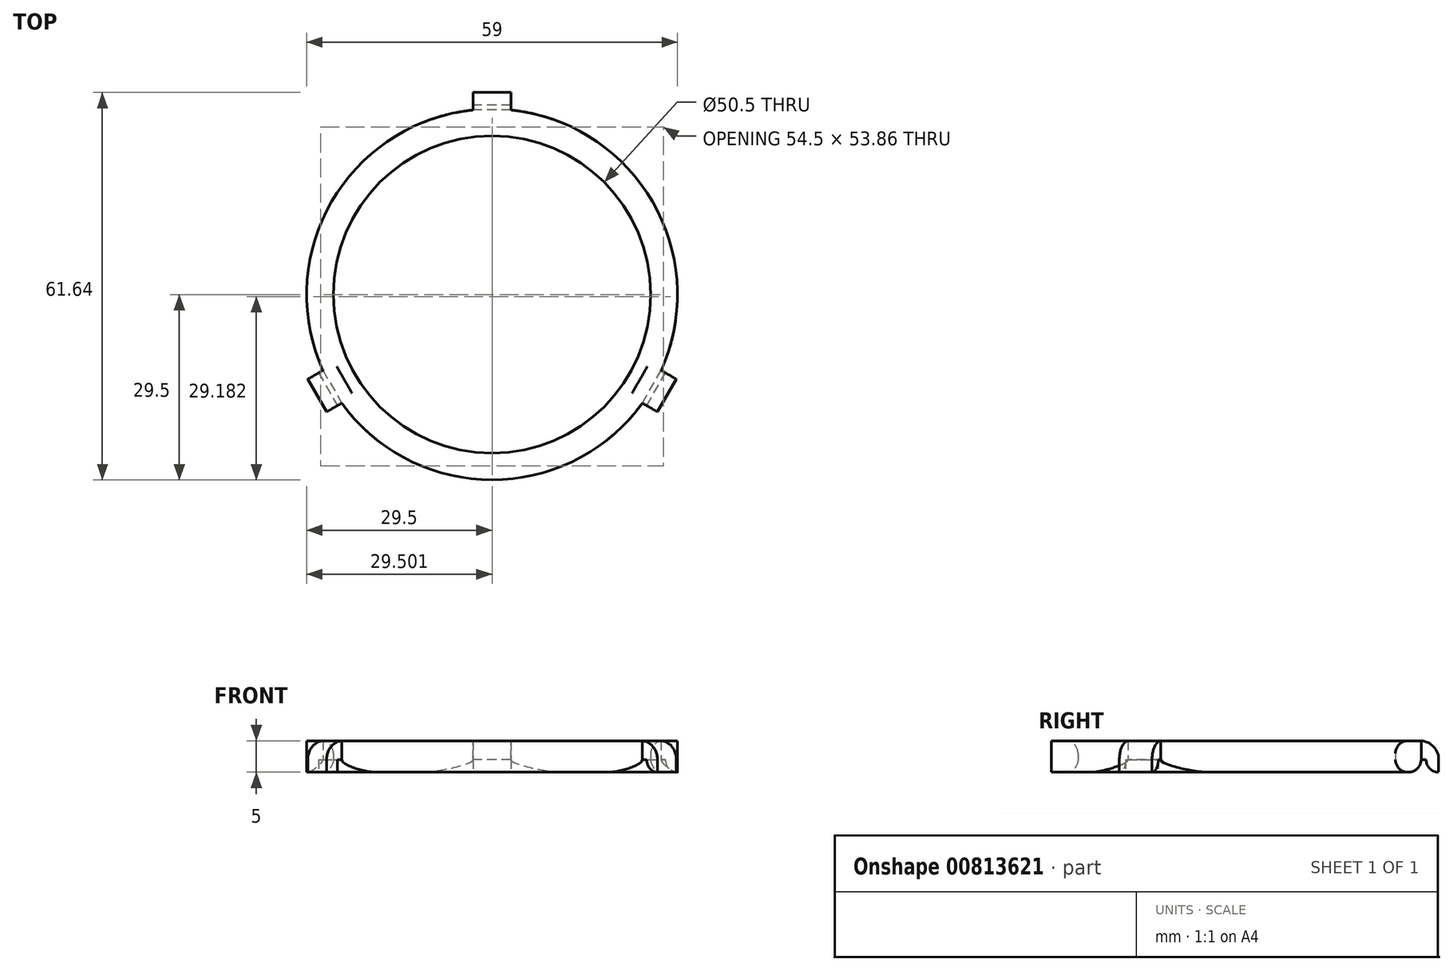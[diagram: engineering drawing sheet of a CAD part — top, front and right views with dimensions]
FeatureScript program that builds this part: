
annotation { "Feature Type Name" : "Feature", "Feature Type Description" : "" }
export const myFeature = defineFeature(function(context is Context, id is Id, definition is map)
    precondition{}
    {
        {
            var Q0;
            Q0=qCreatedBy(makeId("Top.planeOp"),FACE);
            var sketch = newSketch(context, id + "F0", { "sketchPlane" : qUnion([Q0])});
            skCircle(sketch, "E0", {"center": v(0, 0) * mm, "radius": 25.25 * mm});
            skCircle(sketch, "E1", {"center": v(0, 0) * mm, "radius": 29.5 * mm});
            skSolve(sketch);
        }
        {
            var Q0;
            Q0 = qSketchRegion(id + "F0", true);
            extrude(context, id + "F1", {"entities" : qUnion([Q0]), "depth" : 5 * mm, "offsetDistance" : 25 * mm});
        }
        {
            var Q0;
            Q0=makeQuery(id+"F1.opExtrude","CAP_EDGE",EDGE,{"disambiguationData":[OSD([sQuery(id+"F0.wireOp",EDGE,"E0")])],"isStart":false});
            var Q1;
            Q1=makeQuery(id+"F1.opExtrude","CAP_EDGE",EDGE,{"disambiguationData":[OSD([sQuery(id+"F0.wireOp",EDGE,"E0")])],"isStart":true});
            fillet(context, id + "F2", {"entities" : qUnion([Q0, Q1]), "radius" : 2 * mm, "tangentPropagation" : true, "allowEdgeOverflow" : false});
        }
        {
            var Q0;
            Q0=qCreatedBy(makeId("Top.planeOp"),FACE);
            var sketch = newSketch(context, id + "F3", { "sketchPlane" : qUnion([Q0])});
            skLineSegment(sketch, "E2.bottom", {"start": v(-3, 32.14) * mm, "end": v(3, 32.14) * mm});
            skLineSegment(sketch, "E2.top", {"start": v(-3, 27.14) * mm, "end": v(3, 27.14) * mm});
            skLineSegment(sketch, "E2.left", {"start": v(-3, 32.14) * mm, "end": v(-3, 27.14) * mm});
            skLineSegment(sketch, "E2.right", {"start": v(3, 32.14) * mm, "end": v(3, 27.14) * mm});
            skLineSegment(sketch, "E3.1.0", {"start": v(-26.33, -18.67) * mm, "end": v(-29.33, -13.47) * mm});
            skLineSegment(sketch, "E3.1.1", {"start": v(-22, -16.17) * mm, "end": v(-25, -10.97) * mm});
            skLineSegment(sketch, "E3.1.2", {"start": v(-26.33, -18.67) * mm, "end": v(-22, -16.17) * mm});
            skLineSegment(sketch, "E3.1.3", {"start": v(-29.33, -13.47) * mm, "end": v(-25, -10.97) * mm});
            skLineSegment(sketch, "E3.2.0", {"start": v(29.33, -13.47) * mm, "end": v(26.33, -18.67) * mm});
            skLineSegment(sketch, "E3.2.1", {"start": v(25, -10.97) * mm, "end": v(22, -16.17) * mm});
            skLineSegment(sketch, "E3.2.2", {"start": v(29.33, -13.47) * mm, "end": v(25, -10.97) * mm});
            skLineSegment(sketch, "E3.2.3", {"start": v(26.33, -18.67) * mm, "end": v(22, -16.17) * mm});
            skPoint(sketch, "E3.center", {"position": v(0, 0) * mm});
            skCircle(sketch, "E4.0", {"center": v(0, 0) * mm, "radius": 29.5 * mm, "construction": true});
            skSolve(sketch);
        }
        {
            var Q0;
            Q0 = qSketchRegion(id + "F3", true);
            extrude(context, id + "F4", {"entities" : qUnion([Q0]), "operationType" : NewBodyOperationType.ADD, "depth" : 5 * mm, "offsetDistance" : 25 * mm});
        }
        {
            var Q0;
            Q0=makeQuery(id+"F4.opExtrude","CAP_EDGE",EDGE,{"disambiguationData":[OSD([sQuery(id+"F3.wireOp",EDGE,"E2.bottom")])],"isStart":false});
            var Q1;
            Q1=makeQuery(id+"F4.opExtrude","CAP_EDGE",EDGE,{"disambiguationData":[OSD([sQuery(id+"F3.wireOp",EDGE,"E3.1.0")])],"isStart":false});
            var Q2;
            Q2=makeQuery(id+"F4.opExtrude","CAP_EDGE",EDGE,{"disambiguationData":[OSD([sQuery(id+"F3.wireOp",EDGE,"E3.2.0")])],"isStart":false});
            fillet(context, id + "F5", {"entities" : qUnion([Q0, Q1, Q2]), "radius" : 3 * mm, "tangentPropagation" : true, "allowEdgeOverflow" : false});
        }
        {
            var Q0;
            Q0=makeQuery(id+"F4.boolean.opBoolean","MERGE",FACE,{"derivedFrom":[makeQuery(id+"F1.opExtrude","CAP_FACE",FACE,{"disambiguationData":[OSD([sQuery(id+"F0.wireOp",EDGE,"E0"),sQuery(id+"F0.wireOp",EDGE,"E1")])],"isStart":true}),makeQuery(id+"F4.opExtrude","CAP_FACE",FACE,{"disambiguationData":[OSD([sQuery(id+"F3.wireOp",EDGE,"E2.bottom"),sQuery(id+"F3.wireOp",EDGE,"E2.top"),sQuery(id+"F3.wireOp",EDGE,"E2.left"),sQuery(id+"F3.wireOp",EDGE,"E2.right")])],"isStart":true}),makeQuery(id+"F4.opExtrude","CAP_FACE",FACE,{"disambiguationData":[OSD([sQuery(id+"F3.wireOp",EDGE,"E3.1.0"),sQuery(id+"F3.wireOp",EDGE,"E3.1.1"),sQuery(id+"F3.wireOp",EDGE,"E3.1.2"),sQuery(id+"F3.wireOp",EDGE,"E3.1.3")])],"isStart":true}),makeQuery(id+"F4.opExtrude","CAP_FACE",FACE,{"disambiguationData":[OSD([sQuery(id+"F3.wireOp",EDGE,"E3.2.0"),sQuery(id+"F3.wireOp",EDGE,"E3.2.1"),sQuery(id+"F3.wireOp",EDGE,"E3.2.2"),sQuery(id+"F3.wireOp",EDGE,"E3.2.3")])],"isStart":true})]});
            var sketch = newSketch(context, id + "F6", { "sketchPlane" : qUnion([Q0])});
            skLineSegment(sketch, "E5.bottom", {"start": v(3, -30.14) * mm, "end": v(-3, -30.14) * mm});
            skLineSegment(sketch, "E5.top", {"start": v(3, -29.35) * mm, "end": v(-3, -29.35) * mm});
            skLineSegment(sketch, "E5.left", {"start": v(3, -30.14) * mm, "end": v(3, -29.35) * mm});
            skLineSegment(sketch, "E5.right", {"start": v(-3, -30.14) * mm, "end": v(-3, -29.35) * mm});
            skLineSegment(sketch, "E6.1.0", {"start": v(23.92, 17.27) * mm, "end": v(26.92, 12.08) * mm});
            skLineSegment(sketch, "E6.1.1", {"start": v(24.6, 17.67) * mm, "end": v(27.6, 12.47) * mm});
            skLineSegment(sketch, "E6.1.2", {"start": v(27.6, 12.47) * mm, "end": v(26.92, 12.08) * mm});
            skLineSegment(sketch, "E6.1.3", {"start": v(24.6, 17.67) * mm, "end": v(23.92, 17.27) * mm});
            skLineSegment(sketch, "E6.2.0", {"start": v(-26.92, 12.08) * mm, "end": v(-23.92, 17.27) * mm});
            skLineSegment(sketch, "E6.2.1", {"start": v(-27.6, 12.47) * mm, "end": v(-24.6, 17.67) * mm});
            skLineSegment(sketch, "E6.2.2", {"start": v(-24.6, 17.67) * mm, "end": v(-23.92, 17.27) * mm});
            skLineSegment(sketch, "E6.2.3", {"start": v(-27.6, 12.47) * mm, "end": v(-26.92, 12.08) * mm});
            skPoint(sketch, "E6.center", {"position": v(0, 0) * mm});
            skSolve(sketch);
        }
        {
            var Q0;
            Q0 = qSketchRegion(id + "F6", true);
            extrude(context, id + "F7", {"entities" : qUnion([Q0]), "operationType" : NewBodyOperationType.REMOVE, "oppositeDirection" : true, "depth" : 2 * mm, "offsetDistance" : 25 * mm});
        }
        {
            var Q0;
            Q0=makeQuery(id+"F7.boolean.opBoolean","COPY",EDGE,{"derivedFrom":makeQuery(id+"F7.opExtrude","CAP_EDGE",EDGE,{"disambiguationData":[OSD([sQuery(id+"F6.wireOp",EDGE,"E5.top")])],"isStart":true})});
            var Q1;
            Q1=makeQuery(id+"F7.boolean.opBoolean","COPY",EDGE,{"derivedFrom":makeQuery(id+"F7.opExtrude","CAP_EDGE",EDGE,{"disambiguationData":[OSD([sQuery(id+"F6.wireOp",EDGE,"E5.bottom")])],"isStart":true})});
            var Q2;
            Q2=makeQuery(id+"F7.boolean.opBoolean","COPY",EDGE,{"derivedFrom":makeQuery(id+"F7.opExtrude","CAP_EDGE",EDGE,{"disambiguationData":[OSD([sQuery(id+"F6.wireOp",EDGE,"E6.1.1")])],"isStart":true})});
            var Q3;
            Q3=makeQuery(id+"F7.boolean.opBoolean","COPY",EDGE,{"derivedFrom":makeQuery(id+"F7.opExtrude","CAP_EDGE",EDGE,{"disambiguationData":[OSD([sQuery(id+"F6.wireOp",EDGE,"E6.1.0")])],"isStart":true})});
            var Q4;
            Q4=makeQuery(id+"F7.boolean.opBoolean","COPY",EDGE,{"derivedFrom":makeQuery(id+"F7.opExtrude","CAP_EDGE",EDGE,{"disambiguationData":[OSD([sQuery(id+"F6.wireOp",EDGE,"E6.2.0")])],"isStart":true})});
            var Q5;
            Q5=makeQuery(id+"F7.boolean.opBoolean","COPY",EDGE,{"derivedFrom":makeQuery(id+"F7.opExtrude","CAP_EDGE",EDGE,{"disambiguationData":[OSD([sQuery(id+"F6.wireOp",EDGE,"E6.2.1")])],"isStart":true})});
            fillet(context, id + "F8", {"entities" : qUnion([Q0, Q1, Q2, Q3, Q4, Q5]), "radius" : 2 * mm, "tangentPropagation" : true, "allowEdgeOverflow" : false});
        }
    });
